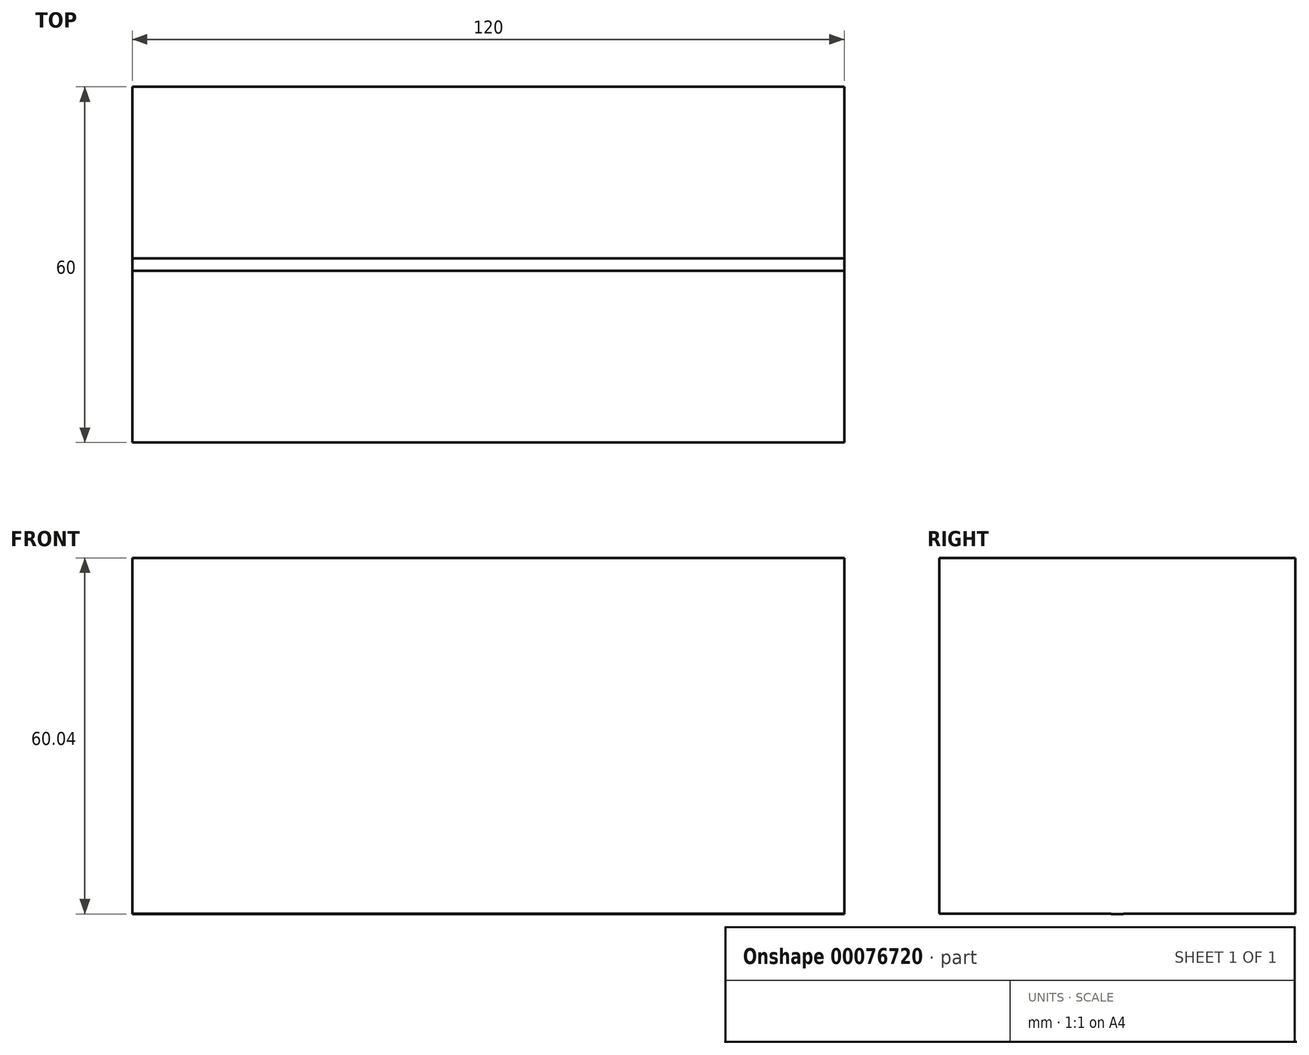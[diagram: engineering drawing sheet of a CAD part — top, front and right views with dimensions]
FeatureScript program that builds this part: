
annotation { "Feature Type Name" : "Feature", "Feature Type Description" : "" }
export const myFeature = defineFeature(function(context is Context, id is Id, definition is map)
    precondition{}
    {
        {
            var Q0;
            Q0=qCreatedBy(makeId("Front.planeOp"),FACE);
            var sketch = newSketch(context, id + "F0", { "sketchPlane" : qUnion([Q0])});
            skLineSegment(sketch, "E0.bottom", {"start": v(-60, -30) * mm, "end": v(60, -30) * mm});
            skLineSegment(sketch, "E0.top", {"start": v(-60, 30) * mm, "end": v(60, 30) * mm});
            skLineSegment(sketch, "E0.left", {"start": v(-60, -30) * mm, "end": v(-60, 30) * mm});
            skLineSegment(sketch, "E0.right", {"start": v(60, -30) * mm, "end": v(60, 30) * mm});
            skPoint(sketch, "E0.middle", {"position": v(0, 0) * mm});
            skSolve(sketch);
        }
        {
            var Q0;
            Q0=makeQuery(id+"F0.imprint","IMPRINT",FACE,{"disambiguationData":[TD([[makeQuery(id+"F0.imprint","IMPRINT",EDGE,{"derivedFrom":sQuery(id+"F0.wireOp",EDGE,"E0.bottom")}),1.0]])]});
            extrude(context, id + "F1", {"entities" : qUnion([Q0]), "endBound" : BoundingType.SYMMETRIC, "depth" : 60 * mm});
        }
        {
            var Q0;
            Q0=qCreatedBy(makeId("Front.planeOp"),FACE);
            var sketch = newSketch(context, id + "F2", { "sketchPlane" : qUnion([Q0])});
            skLineSegment(sketch, "E1.bottom", {"start": v(60, 27.3) * mm, "end": v(-60, 27.3) * mm});
            skLineSegment(sketch, "E1.top", {"start": v(60, 30.02) * mm, "end": v(-60, 30.02) * mm});
            skLineSegment(sketch, "E1.left", {"start": v(60, 27.3) * mm, "end": v(60, 30.02) * mm});
            skLineSegment(sketch, "E1.right", {"start": v(-60, 27.3) * mm, "end": v(-60, 30.02) * mm});
            skPoint(sketch, "E1.middle", {"position": v(0, 28.66) * mm});
            skLineSegment(sketch, "E2.bottom", {"start": v(60, -30.02) * mm, "end": v(-60, -30.02) * mm});
            skLineSegment(sketch, "E2.top", {"start": v(60, -27.3) * mm, "end": v(-60, -27.3) * mm});
            skLineSegment(sketch, "E2.left", {"start": v(60, -30.02) * mm, "end": v(60, -27.3) * mm});
            skLineSegment(sketch, "E2.right", {"start": v(-60, -30.02) * mm, "end": v(-60, -27.3) * mm});
            skPoint(sketch, "E2.middle", {"position": v(0, -28.66) * mm});
            skLineSegment(sketch, "E3.bottom", {"start": v(59.72, -27.3) * mm, "end": v(55.39, -27.3) * mm});
            skLineSegment(sketch, "E3.top", {"start": v(59.72, 27.3) * mm, "end": v(55.39, 27.3) * mm});
            skLineSegment(sketch, "E3.left", {"start": v(59.72, -27.3) * mm, "end": v(59.72, 27.3) * mm});
            skLineSegment(sketch, "E3.right", {"start": v(55.39, -27.3) * mm, "end": v(55.39, 27.3) * mm});
            skPoint(sketch, "E3.middle", {"position": v(57.55, 0) * mm});
            skLineSegment(sketch, "E4.bottom", {"start": v(-60, 27.3) * mm, "end": v(-55.7, 27.3) * mm});
            skLineSegment(sketch, "E4.top", {"start": v(-60, -27.3) * mm, "end": v(-55.7, -27.3) * mm});
            skLineSegment(sketch, "E4.left", {"start": v(-60, 27.3) * mm, "end": v(-60, -27.3) * mm});
            skLineSegment(sketch, "E4.right", {"start": v(-55.7, 27.3) * mm, "end": v(-55.7, -27.3) * mm});
            skPoint(sketch, "E4.middle", {"position": v(-57.85, 0) * mm});
            skSolve(sketch);
        }
        {
            var Q0;
            Q0 = qSketchRegion(id + "F2", true);
            extrude(context, id + "F3", {"entities" : qUnion([Q0]), "operationType" : NewBodyOperationType.ADD, "endBound" : BoundingType.SYMMETRIC, "depth" : 2.1 * mm});
        }
    });
